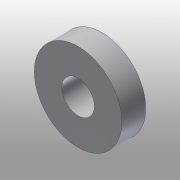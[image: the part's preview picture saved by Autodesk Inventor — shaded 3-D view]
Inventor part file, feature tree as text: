
AUTODESK INVENTOR PART (.ipt)
format: ipt  version: 2016 (Build 200138000, 138)  size: 85,504 bytes
history: native  units: mm
features: extrude x1, sketch x1
ambient origin geometry x8: Origin, YZ Plane, XZ Plane, XY Plane, X Axis, Y Axis, Z Axis, Center Point
bodies: Solid1 (feature_tree)
feature tree (2):
  extrude  "Extrusion1"  Depth=3.0mm
  sketch  "Sketch1"  dims[d0=11.0mm d1=4.1mm d2=3.0mm d3=0.0mm]
